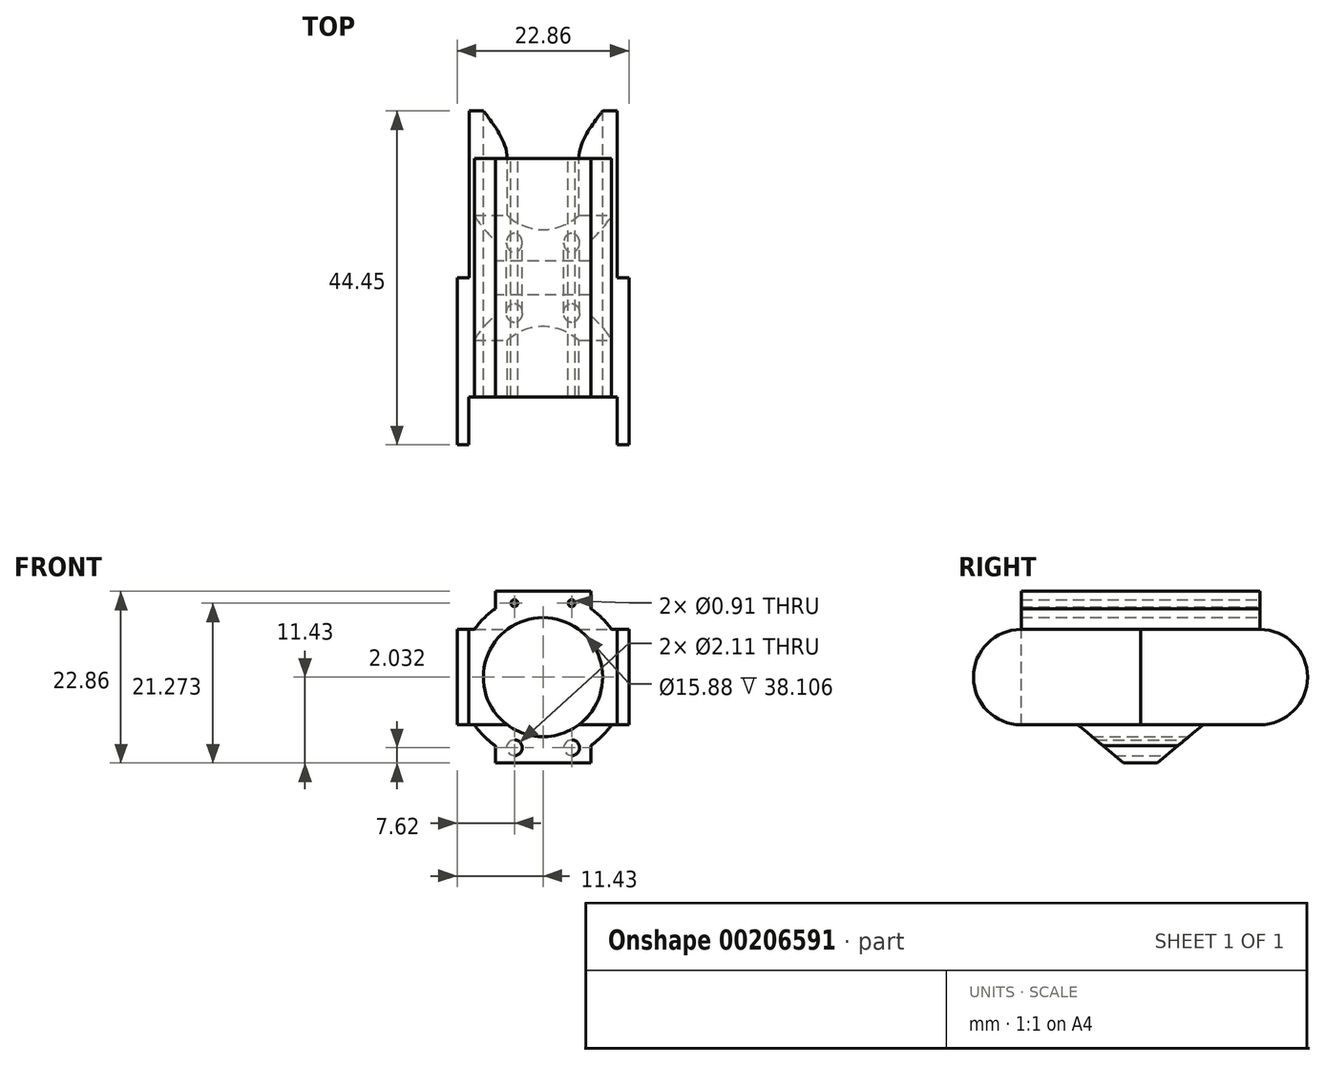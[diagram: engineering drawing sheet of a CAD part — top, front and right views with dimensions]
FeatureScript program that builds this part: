
annotation { "Feature Type Name" : "Feature", "Feature Type Description" : "" }
export const myFeature = defineFeature(function(context is Context, id is Id, definition is map)
    precondition{}
    {
        {
            var Q0;
            Q0=qCreatedBy(makeId("Front.planeOp"),FACE);
            var sketch = newSketch(context, id + "F0", { "sketchPlane" : qUnion([Q0])});
            skCircle(sketch, "E0", {"center": v(0, 0) * mm, "radius": 7.94 * mm});
            skArc(sketch, "E1", {"start": v(-6.35, 9.12) * mm, "mid": v(-7.86, 7.86) * mm, "end": v(-9.12, 6.35) * mm});
            skLineSegment(sketch, "E2", {"start": v(0, 14.87) * mm, "end": v(0, -18.92) * mm, "construction": true});
            skLineSegment(sketch, "E3", {"start": v(-17.83, 0) * mm, "end": v(15.9, 0) * mm, "construction": true});
            skLineSegment(sketch, "E4.bottom", {"start": v(-6.35, 11.43) * mm, "end": v(6.35, 11.43) * mm});
            skLineSegment(sketch, "E4.top", {"start": v(-6.35, 8.26) * mm, "end": v(6.35, 8.26) * mm});
            skLineSegment(sketch, "E4.left", {"start": v(-6.35, 11.43) * mm, "end": v(-6.35, 8.26) * mm});
            skLineSegment(sketch, "E4.right", {"start": v(6.35, 11.43) * mm, "end": v(6.35, 8.26) * mm});
            skPoint(sketch, "E5.firstSnap0", {"position": v(6.35, 9.84) * mm});
            skPoint(sketch, "E5.oppositeSnap0", {"position": v(-6.35, 9.84) * mm});
            skLineSegment(sketch, "E5.bottom", {"start": v(6.35, -8.26) * mm, "end": v(-6.35, -8.26) * mm});
            skLineSegment(sketch, "E5.top", {"start": v(6.35, -11.43) * mm, "end": v(-6.35, -11.43) * mm});
            skLineSegment(sketch, "E5.left", {"start": v(6.35, -8.26) * mm, "end": v(6.35, -11.43) * mm});
            skLineSegment(sketch, "E5.right", {"start": v(-6.35, -8.26) * mm, "end": v(-6.35, -11.43) * mm});
            skLineSegment(sketch, "E6.bottom", {"start": v(-11.43, 6.35) * mm, "end": v(-8.26, 6.35) * mm});
            skLineSegment(sketch, "E6.top", {"start": v(-11.43, -6.35) * mm, "end": v(-8.26, -6.35) * mm});
            skLineSegment(sketch, "E6.left", {"start": v(-11.43, 6.35) * mm, "end": v(-11.43, -6.35) * mm});
            skLineSegment(sketch, "E6.right", {"start": v(-8.26, 6.35) * mm, "end": v(-8.26, -6.35) * mm});
            skPoint(sketch, "E7.firstSnap0", {"position": v(-9.84, 6.35) * mm});
            skLineSegment(sketch, "E7.bottom", {"start": v(11.43, 6.35) * mm, "end": v(8.26, 6.35) * mm});
            skLineSegment(sketch, "E7.top", {"start": v(11.43, -6.35) * mm, "end": v(8.26, -6.35) * mm});
            skLineSegment(sketch, "E7.left", {"start": v(11.43, 6.35) * mm, "end": v(11.43, -6.35) * mm});
            skLineSegment(sketch, "E7.right", {"start": v(8.26, 6.35) * mm, "end": v(8.26, -6.35) * mm});
            skArc(sketch, "E8.trimOffspring", {"start": v(-9.12, -6.35) * mm, "mid": v(-7.86, -7.86) * mm, "end": v(-6.35, -9.12) * mm});
            skArc(sketch, "E9.trimOffspring", {"start": v(6.35, -9.12) * mm, "mid": v(7.86, -7.86) * mm, "end": v(9.12, -6.35) * mm});
            skArc(sketch, "E10.trimOffspring", {"start": v(9.12, 6.35) * mm, "mid": v(7.86, 7.86) * mm, "end": v(6.35, 9.12) * mm});
            skLineSegment(sketch, "E11", {"start": v(-3.8, 12.68) * mm, "end": v(-3.8, -13.54) * mm, "construction": true});
            skLineSegment(sketch, "E12", {"start": v(3.81, 12.6) * mm, "end": v(3.81, -13.1) * mm, "construction": true});
            skLineSegment(sketch, "E13", {"start": v(-8.15, 9.84) * mm, "end": v(7.52, 9.84) * mm, "construction": true});
            skPoint(sketch, "E14.startSnap0", {"position": v(-6.35, -9.84) * mm});
            skCircle(sketch, "E15", {"center": v(-3.8, 9.84) * mm, "radius": 0.46 * mm});
            skCircle(sketch, "E16", {"center": v(3.81, 9.84) * mm, "radius": 0.46 * mm});
            skCircle(sketch, "E17", {"center": v(-3.8, -9.4) * mm, "radius": 1.05 * mm});
            skLineSegment(sketch, "E18", {"start": v(-5.52, -9.4) * mm, "end": v(5.27, -9.4) * mm, "construction": true});
            skCircle(sketch, "E19", {"center": v(3.81, -9.4) * mm, "radius": 1.05 * mm});
            skSolve(sketch);
        }
        {
            var Q0;
            Q0 = qSketchRegion(id + "F0", true);
            extrude(context, id + "F1", {"entities" : qUnion([Q0]), "depth" : 50.8 * mm});
        }
        {
            var Q0;
            Q0=makeQuery(id+"F1.opExtrude","SWEPT_FACE",FACE,{"disambiguationData":[OSD([sQuery(id+"F0.wireOp",EDGE,"E7.left")])]});
            var sketch = newSketch(context, id + "F2", { "sketchPlane" : qUnion([Q0])});
            skLineSegment(sketch, "E20", {"start": v(-36.28, 0) * mm, "end": v(3.87, 0) * mm, "construction": true});
            skLineSegment(sketch, "E21", {"start": v(3.87, 0) * mm, "end": v(-6.35, 8.67) * mm, "construction": true});
            skLineSegment(sketch, "E22", {"start": v(-6.35, 8.67) * mm, "end": v(-6.35, -9.25) * mm, "construction": true});
            skLineSegment(sketch, "E23", {"start": v(-6.35, -9.25) * mm, "end": v(-38.1, 9.4) * mm, "construction": true});
            skLineSegment(sketch, "E24", {"start": v(-38.1, 9.4) * mm, "end": v(-38.1, -10.05) * mm, "construction": true});
            skCircle(sketch, "E25", {"center": v(-6.35, 0) * mm, "radius": 6.35 * mm});
            skCircle(sketch, "E26", {"center": v(-38.1, 0) * mm, "radius": 6.35 * mm});
            skLineSegment(sketch, "E27", {"start": v(-6.35, 6.35) * mm, "end": v(-6.35, 16.95) * mm});
            skLineSegment(sketch, "E28", {"start": v(-6.35, 16.95) * mm, "end": v(6.57, 16.95) * mm});
            skLineSegment(sketch, "E29", {"start": v(6.57, 16.95) * mm, "end": v(6.57, -14.26) * mm});
            skLineSegment(sketch, "E30", {"start": v(6.57, -14.26) * mm, "end": v(-6.35, -14.26) * mm});
            skLineSegment(sketch, "E31", {"start": v(-6.35, -14.26) * mm, "end": v(-6.35, -6.35) * mm});
            skLineSegment(sketch, "E32", {"start": v(-6.35, 0) * mm, "end": v(-23.35, -14.26) * mm});
            skLineSegment(sketch, "E33", {"start": v(-23.35, -14.26) * mm, "end": v(-6.35, -14.26) * mm});
            skLineSegment(sketch, "E34", {"start": v(-38.1, 6.35) * mm, "end": v(-38.1, 21.27) * mm});
            skLineSegment(sketch, "E35", {"start": v(-38.1, 21.27) * mm, "end": v(-58.9, 21.27) * mm});
            skLineSegment(sketch, "E36", {"start": v(-58.9, 21.27) * mm, "end": v(-58.9, -13.1) * mm});
            skLineSegment(sketch, "E37", {"start": v(-58.9, -13.1) * mm, "end": v(-38.1, -13.1) * mm});
            skLineSegment(sketch, "E38", {"start": v(-38.1, -13.1) * mm, "end": v(-38.1, -6.35) * mm});
            skLineSegment(sketch, "E39", {"start": v(-38.1, 0) * mm, "end": v(-22.5, -13.1) * mm});
            skLineSegment(sketch, "E40", {"start": v(-22.5, -13.1) * mm, "end": v(-38.1, -13.1) * mm});
            skLineSegment(sketch, "E41", {"start": v(-38.1, -6.35) * mm, "end": v(-30.53, -6.35) * mm});
            skLineSegment(sketch, "E42", {"start": v(-6.35, -6.35) * mm, "end": v(-13.92, -6.35) * mm});
            skSolve(sketch);
        }
        {
            var Q0;
            Q0=makeQuery(id+"F2.imprint","IMPRINT",FACE,{"disambiguationData":[TD([[makeQuery(id+"F2.imprint","IMPRINT",EDGE,{"derivedFrom":sQuery(id+"F2.wireOp",EDGE,"E31")}),1.0]])]});
            var Q1;
            Q1=makeQuery(id+"F2.imprint","IMPRINT",FACE,{"disambiguationData":[TD([[makeQuery(id+"F2.imprint","IMPRINT",EDGE,{"derivedFrom":sQuery(id+"F2.wireOp",EDGE,"E38")}),-1.0]])]});
            var Q2;
            {var subQ0=sQuery(id+"F2.wireOp",EDGE,"E25");var subQ1=sQuery(id+"F0.wireOp",EDGE,"E7.left");var subQ4=makeQuery(id+"F1.opExtrude","CAP_EDGE",EDGE,{"disambiguationData":[OSD([subQ1])],"isStart":true});var subQ5=makeQuery(id+"F2.imprint","INTERSECT",VERTEX,{"derivedFrom":[subQ4,subQ0]});Q2=makeQuery(id+"F2.imprint","IMPRINT",FACE,{"disambiguationData":[TD([[makeQuery(id+"F2.imprint","IMPRINT",EDGE,{"disambiguationData":[TD([[subQ5,1.0]])],"derivedFrom":subQ4}),-1.0]])]});}
            var Q3;
            {var subQ0=sQuery(id+"F2.wireOp",EDGE,"E25");var subQ1=sQuery(id+"F0.wireOp",EDGE,"E7.left");var subQ4=makeQuery(id+"F1.opExtrude","CAP_EDGE",EDGE,{"disambiguationData":[OSD([subQ1])],"isStart":true});var subQ5=makeQuery(id+"F2.imprint","INTERSECT",VERTEX,{"derivedFrom":[subQ4,subQ0]});Q3=makeQuery(id+"F2.imprint","IMPRINT",FACE,{"disambiguationData":[TD([[makeQuery(id+"F2.imprint","IMPRINT",EDGE,{"disambiguationData":[TD([[subQ5,-1.0]])],"derivedFrom":subQ4}),-1.0]])]});}
            var Q4;
            {var subQ1=sQuery(id+"F0.wireOp",EDGE,"E7.left");var subQ6=makeQuery(id+"F1.opExtrude","CAP_EDGE",EDGE,{"disambiguationData":[OSD([subQ1])],"isStart":false});Q4=makeQuery(id+"F2.imprint","IMPRINT",FACE,{"disambiguationData":[TD([[makeQuery(id+"F2.imprint","IMPRINT",EDGE,{"derivedFrom":subQ6}),1.0]])]});}
            var Q5;
            {var subQ0=sQuery(id+"F2.wireOp",EDGE,"E34");Q5=makeQuery(id+"F2.imprint","IMPRINT",FACE,{"disambiguationData":[TD([[makeQuery(id+"F2.imprint","IMPRINT",EDGE,{"derivedFrom":subQ0}),1.0]])]});}
            var Q6;
            {var subQ0=sQuery(id+"F2.wireOp",EDGE,"E27");Q6=makeQuery(id+"F2.imprint","IMPRINT",FACE,{"disambiguationData":[TD([[makeQuery(id+"F2.imprint","IMPRINT",EDGE,{"derivedFrom":subQ0}),-1.0]])]});}
            extrude(context, id + "F3", {"entities" : qUnion([Q0, Q1, Q2, Q3, Q4, Q5, Q6]), "operationType" : NewBodyOperationType.REMOVE, "oppositeDirection" : true, "depth" : 25.4 * mm});
        }
        {
            var Q0;
            Q0=makeQuery(id+"F1.opExtrude","SWEPT_FACE",FACE,{"disambiguationData":[OSD([sQuery(id+"F0.wireOp",EDGE,"E7.left")])]});
            var sketch = newSketch(context, id + "F4", { "sketchPlane" : qUnion([Q0])});
            skCircle(sketch, "E43", {"center": v(-6.35, 0) * mm, "radius": 6.35 * mm});
            skLineSegment(sketch, "E44.bottom", {"start": v(-6.35, 6.35) * mm, "end": v(-22.23, 6.35) * mm});
            skLineSegment(sketch, "E44.top", {"start": v(-6.35, 6.35) * mm, "end": v(-22.23, 6.35) * mm});
            skLineSegment(sketch, "E44.left", {"start": v(-6.35, 6.35) * mm, "end": v(-6.35, 6.35) * mm});
            skLineSegment(sketch, "E44.right", {"start": v(-22.23, 6.35) * mm, "end": v(-22.23, 6.35) * mm});
            skLineSegment(sketch, "E45.top", {"start": v(-22.23, -6.35) * mm, "end": v(-22.23, -6.35) * mm});
            skLineSegment(sketch, "E45.left", {"start": v(-22.23, 6.35) * mm, "end": v(-22.23, -6.35) * mm});
            skLineSegment(sketch, "E45.right", {"start": v(-22.23, 6.35) * mm, "end": v(-22.23, -6.35) * mm});
            skLineSegment(sketch, "E46", {"start": v(-22.23, -6.35) * mm, "end": v(-6.35, -6.35) * mm});
            skSolve(sketch);
        }
        {
            var Q0;
            Q0 = qSketchRegion(id + "F4", true);
            extrude(context, id + "F5", {"entities" : qUnion([Q0]), "operationType" : NewBodyOperationType.REMOVE, "oppositeDirection" : true, "depth" : 1.59 * mm});
        }
        {
            var Q0;
            Q0=makeQuery(id+"F1.opExtrude","SWEPT_FACE",FACE,{"disambiguationData":[OSD([sQuery(id+"F0.wireOp",EDGE,"E6.left")])]});
            var sketch = newSketch(context, id + "F6", { "sketchPlane" : qUnion([Q0])});
            skCircle(sketch, "E47", {"center": v(6.35, 0) * mm, "radius": 6.35 * mm});
            skLineSegment(sketch, "E48.bottom", {"start": v(6.35, 6.35) * mm, "end": v(22.23, 6.35) * mm});
            skLineSegment(sketch, "E48.top", {"start": v(6.35, -6.35) * mm, "end": v(22.23, -6.35) * mm});
            skLineSegment(sketch, "E48.left", {"start": v(6.35, 6.35) * mm, "end": v(6.35, -6.35) * mm});
            skLineSegment(sketch, "E48.right", {"start": v(22.23, 6.35) * mm, "end": v(22.23, -6.35) * mm});
            skSolve(sketch);
        }
        {
            var Q0;
            Q0 = qSketchRegion(id + "F6", true);
            extrude(context, id + "F7", {"entities" : qUnion([Q0]), "operationType" : NewBodyOperationType.REMOVE, "oppositeDirection" : true, "depth" : 1.59 * mm});
        }
        {
            var Q0;
            Q0=makeQuery(id+"F1.opExtrude","SWEPT_FACE",FACE,{"disambiguationData":[OSD([sQuery(id+"F0.wireOp",EDGE,"E7.bottom")])]});
            var sketch = newSketch(context, id + "F8", { "sketchPlane" : qUnion([Q0])});
            skLineSegment(sketch, "E49.bottom", {"start": v(9.84, -38.1) * mm, "end": v(-9.86, -38.1) * mm});
            skLineSegment(sketch, "E49.top", {"start": v(9.84, -48.54) * mm, "end": v(-9.86, -48.54) * mm});
            skLineSegment(sketch, "E49.left", {"start": v(9.84, -38.1) * mm, "end": v(9.84, -48.54) * mm});
            skLineSegment(sketch, "E49.right", {"start": v(-9.86, -38.1) * mm, "end": v(-9.86, -48.54) * mm});
            skLineSegment(sketch, "E50.bottom", {"start": v(11.43, -38.1) * mm, "end": v(9.84, -38.1) * mm, "construction": true});
            skLineSegment(sketch, "E50.top", {"start": v(11.43, -48.54) * mm, "end": v(9.84, -48.54) * mm, "construction": true});
            skLineSegment(sketch, "E50.left", {"start": v(11.43, -38.1) * mm, "end": v(11.43, -48.54) * mm, "construction": true});
            skLineSegment(sketch, "E50.right", {"start": v(9.84, -38.1) * mm, "end": v(9.84, -48.54) * mm, "construction": true});
            skLineSegment(sketch, "E51.bottom", {"start": v(-9.86, -38.1) * mm, "end": v(-11.4, -38.1) * mm, "construction": true});
            skLineSegment(sketch, "E51.top", {"start": v(-9.86, -48.54) * mm, "end": v(-11.4, -48.54) * mm, "construction": true});
            skLineSegment(sketch, "E51.left", {"start": v(-9.86, -38.1) * mm, "end": v(-9.86, -48.54) * mm, "construction": true});
            skLineSegment(sketch, "E51.right", {"start": v(-11.4, -38.1) * mm, "end": v(-11.4, -48.54) * mm, "construction": true});
            skLineSegment(sketch, "E52", {"start": v(0, -50.78) * mm, "end": v(0, -31.37) * mm, "construction": true});
            skSolve(sketch);
        }
        {
            var Q0;
            Q0=makeQuery(id+"F8.imprint","IMPRINT",FACE,{"disambiguationData":[TD([[makeQuery(id+"F8.imprint","IMPRINT",EDGE,{"derivedFrom":sQuery(id+"F8.wireOp",EDGE,"E49.top")}),-1.0]])]});
            extrude(context, id + "F9", {"entities" : qUnion([Q0]), "operationType" : NewBodyOperationType.REMOVE, "oppositeDirection" : true, "depth" : 25.4 * mm});
        }
    });
